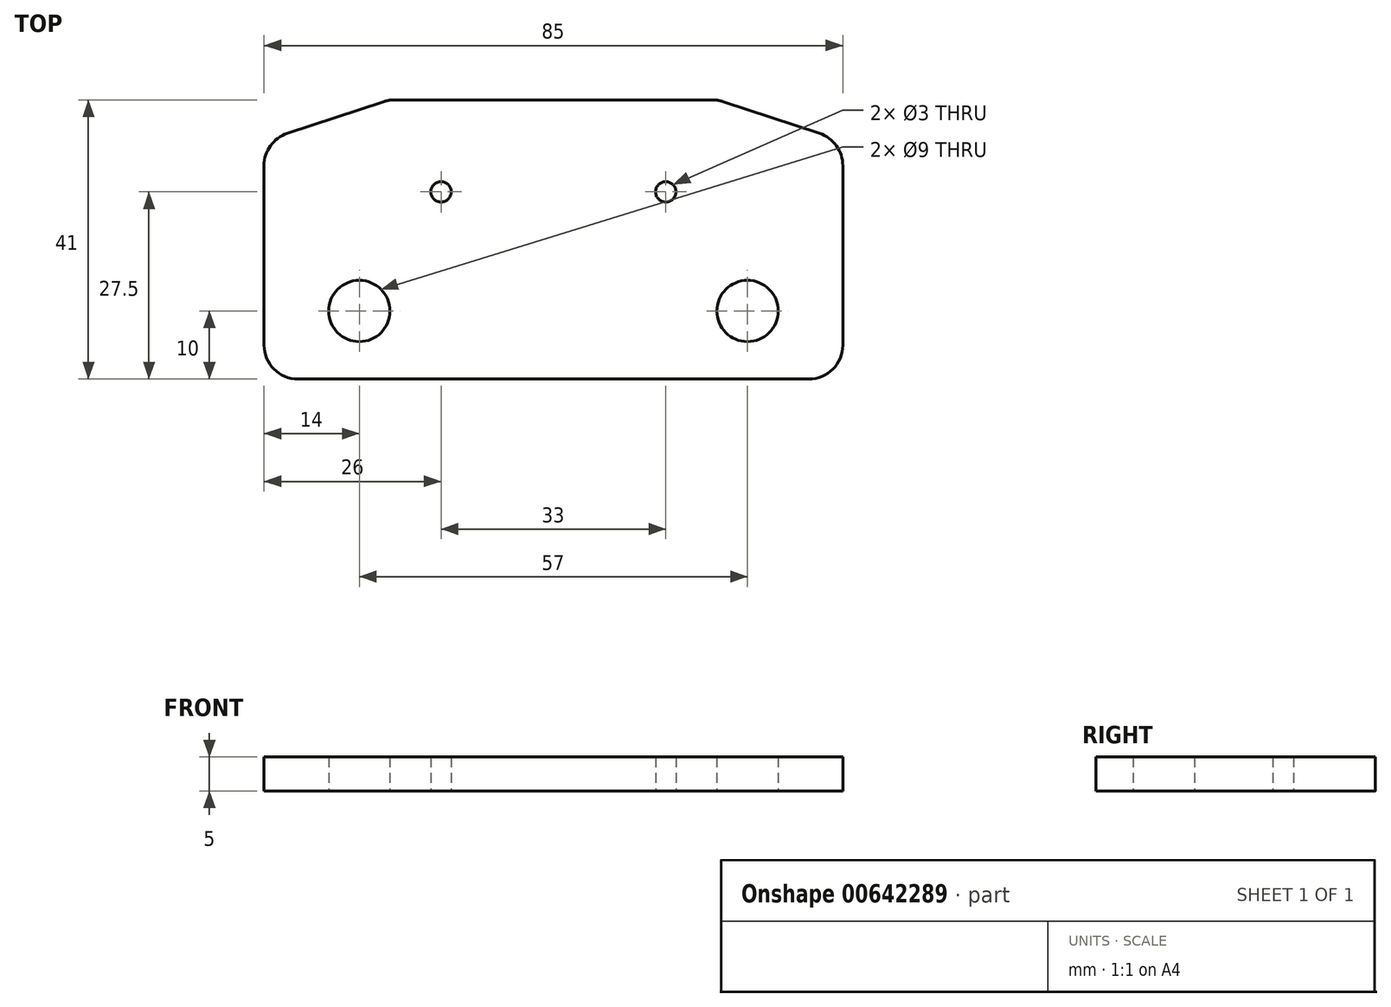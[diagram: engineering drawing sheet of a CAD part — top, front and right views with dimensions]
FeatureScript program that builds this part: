
annotation { "Feature Type Name" : "Feature", "Feature Type Description" : "" }
export const myFeature = defineFeature(function(context is Context, id is Id, definition is map)
    precondition{}
    {
        {
            var Q0;
            Q0=qCreatedBy(makeId("Top.planeOp"),FACE);
            var sketch = newSketch(context, id + "F0", { "sketchPlane" : qUnion([Q0])});
            skPoint(sketch, "E0.middle", {"position": v(0, 0) * mm});
            skLineSegment(sketch, "E1.bottom", {"start": v(37.5, -27.5) * mm, "end": v(-37.5, -27.5) * mm});
            skLineSegment(sketch, "E1.left", {"start": v(42.5, -22.5) * mm, "end": v(42.5, 3.83) * mm});
            skLineSegment(sketch, "E1.right", {"start": v(-42.5, -22.5) * mm, "end": v(-42.5, 3.83) * mm});
            skCircle(sketch, "E2", {"center": v(16.5, 0) * mm, "radius": 1.5 * mm});
            skPoint(sketch, "E2.centerSnap0", {"position": v(20.5, 0) * mm});
            skCircle(sketch, "E3.MirrorC", {"center": v(-16.5, 0) * mm, "radius": 1.5 * mm});
            skCircle(sketch, "E4", {"center": v(28.5, -17.5) * mm, "radius": 4.5 * mm});
            skCircle(sketch, "E5.MirrorC", {"center": v(-28.5, -17.5) * mm, "radius": 4.5 * mm});
            skPoint(sketch, "E6.visualSharp", {"position": v(-42.5, 27.5) * mm});
            skPoint(sketch, "E7.visualSharp", {"position": v(42.5, 27.5) * mm});
            skPoint(sketch, "E8.visualSharp", {"position": v(42.5, -27.5) * mm});
            skArc(sketch, "E8.filletArc", {"start": v(37.5, -27.5) * mm, "mid": v(41.04, -26.04) * mm, "end": v(42.5, -22.5) * mm});
            skPoint(sketch, "E9.visualSharp", {"position": v(-42.5, -27.5) * mm});
            skArc(sketch, "E9.filletArc", {"start": v(-42.5, -22.5) * mm, "mid": v(-41.04, -26.04) * mm, "end": v(-37.5, -27.5) * mm});
            skLineSegment(sketch, "E10", {"start": v(0, 13.5) * mm, "end": v(23.35, 13.5) * mm});
            skLineSegment(sketch, "E11", {"start": v(24.91, 13.25) * mm, "end": v(39.07, 8.58) * mm});
            skLineSegment(sketch, "E12.MirrorCS", {"start": v(0, 13.5) * mm, "end": v(-23.35, 13.5) * mm});
            skLineSegment(sketch, "E13.MirrorCS", {"start": v(-24.91, 13.25) * mm, "end": v(-39.07, 8.58) * mm});
            skPoint(sketch, "E14.visualSharp", {"position": v(-42.5, 7.45) * mm});
            skArc(sketch, "E14.filletArc", {"start": v(-39.07, 8.58) * mm, "mid": v(-41.55, 6.76) * mm, "end": v(-42.5, 3.83) * mm});
            skPoint(sketch, "E15.visualSharp", {"position": v(-24.15, 13.5) * mm});
            skArc(sketch, "E15.filletArc", {"start": v(-23.35, 13.5) * mm, "mid": v(-24.14, 13.44) * mm, "end": v(-24.91, 13.25) * mm});
            skPoint(sketch, "E16.visualSharp", {"position": v(24.15, 13.5) * mm});
            skArc(sketch, "E16.filletArc", {"start": v(24.91, 13.25) * mm, "mid": v(24.14, 13.44) * mm, "end": v(23.35, 13.5) * mm});
            skPoint(sketch, "E17.visualSharp", {"position": v(42.5, 7.45) * mm});
            skArc(sketch, "E17.filletArc", {"start": v(42.5, 3.83) * mm, "mid": v(41.55, 6.76) * mm, "end": v(39.07, 8.58) * mm});
            skPoint(sketch, "E18.orphan", {"position": v(20.5, 7.5) * mm});
            skPoint(sketch, "E0.left.start.orphan", {"position": v(20.5, -7.5) * mm});
            skPoint(sketch, "E0.right.end.orphan", {"position": v(-20.5, 7.5) * mm});
            skPoint(sketch, "E0.right.start.orphan", {"position": v(-20.5, -7.5) * mm});
            skSolve(sketch);
        }
        {
            var Q0;
            Q0=makeQuery(id+"F0.imprint","IMPRINT",FACE,{"disambiguationData":[TD([[makeQuery(id+"F0.imprint","IMPRINT",EDGE,{"derivedFrom":sQuery(id+"F0.wireOp",EDGE,"E1.bottom")}),-1.0]])]});
            extrude(context, id + "F1", {"entities" : qUnion([Q0]), "depth" : 5 * mm, "offsetDistance" : 25 * mm});
        }
    });
